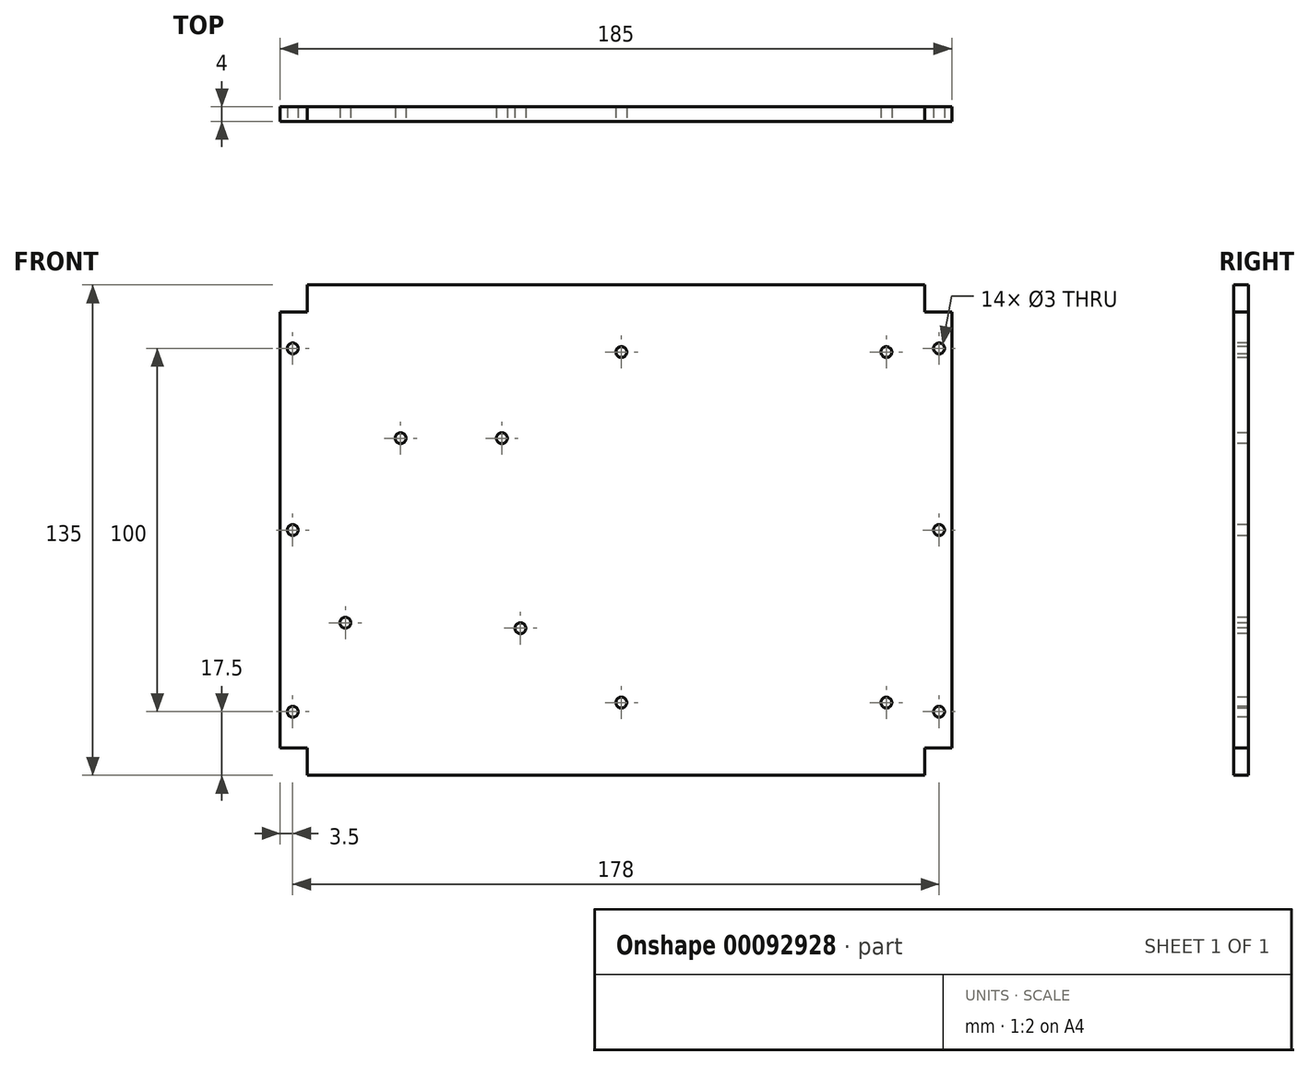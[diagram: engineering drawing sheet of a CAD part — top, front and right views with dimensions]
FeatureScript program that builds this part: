
annotation { "Feature Type Name" : "Feature", "Feature Type Description" : "" }
export const myFeature = defineFeature(function(context is Context, id is Id, definition is map)
    precondition{}
    {
        {
            var Q0;
            Q0=qCreatedBy(makeId("Front.planeOp"),FACE);
            var sketch = newSketch(context, id + "F0", { "sketchPlane" : qUnion([Q0])});
            skLineSegment(sketch, "E0.bottom", {"start": v(5, 0) * mm, "end": v(180, 0) * mm});
            skLineSegment(sketch, "E0.top", {"start": v(5, 135) * mm, "end": v(180, 135) * mm});
            skLineSegment(sketch, "E0.left", {"start": v(0, 5) * mm, "end": v(0, 130) * mm});
            skLineSegment(sketch, "E0.right", {"start": v(185, 5) * mm, "end": v(185, 130) * mm});
            skPoint(sketch, "E1.visualSharp", {"position": v(0, 135) * mm});
            skArc(sketch, "E1.filletArc", {"start": v(5, 135) * mm, "mid": v(1.46, 133.54) * mm, "end": v(0, 130) * mm});
            skPoint(sketch, "E2.visualSharp", {"position": v(185, 135) * mm});
            skArc(sketch, "E2.filletArc", {"start": v(185, 130) * mm, "mid": v(183.54, 133.54) * mm, "end": v(180, 135) * mm});
            skPoint(sketch, "E3.visualSharp", {"position": v(185, 0) * mm});
            skArc(sketch, "E3.filletArc", {"start": v(180, 0) * mm, "mid": v(183.54, 1.46) * mm, "end": v(185, 5) * mm});
            skPoint(sketch, "E4.visualSharp", {"position": v(0, 0) * mm});
            skArc(sketch, "E4.filletArc", {"start": v(0, 5) * mm, "mid": v(1.46, 1.46) * mm, "end": v(5, 0) * mm});
            skLineSegment(sketch, "E5", {"start": v(0, 67.5) * mm, "end": v(185, 67.5) * mm, "construction": true});
            skLineSegment(sketch, "E6", {"start": v(0, 127.5) * mm, "end": v(185, 127.5) * mm});
            skLineSegment(sketch, "E7", {"start": v(0, 7.5) * mm, "end": v(185, 7.5) * mm});
            skLineSegment(sketch, "E8", {"start": v(7.5, 135) * mm, "end": v(7.5, 0) * mm});
            skLineSegment(sketch, "E9", {"start": v(177.5, 135) * mm, "end": v(177.5, 0) * mm});
            skLineSegment(sketch, "E10", {"start": v(92.5, 135) * mm, "end": v(92.5, 0) * mm, "construction": true});
            skSolve(sketch);
        }
        {
            var Q0;
            Q0=makeQuery(id+"F0.imprint","IMPRINT",FACE,{"disambiguationData":[TD([[makeQuery(id+"F0.imprint","IMPRINT",EDGE,{"derivedFrom":sQuery(id+"F0.wireOp",EDGE,"E0.bottom")}),1.0]])]});
            var Q1;
            {var subQ0=sQuery(id+"F0.wireOp",EDGE,"E8");var subQ1=sQuery(id+"F0.wireOp",EDGE,"E6");var subQ2=makeQuery(id+"F0.imprint","INTERSECT",VERTEX,{"derivedFrom":[subQ1,subQ0]});Q1=makeQuery(id+"F0.imprint","IMPRINT",FACE,{"disambiguationData":[TD([[makeQuery(id+"F0.imprint","IMPRINT",EDGE,{"disambiguationData":[TD([[subQ2,-1.0]])],"derivedFrom":subQ1}),-1.0]])]});}
            var Q2;
            {var subQ0=sQuery(id+"F0.wireOp",EDGE,"E8");var subQ1=sQuery(id+"F0.wireOp",EDGE,"E0.top");var subQ2=makeQuery(id+"F0.imprint","INTERSECT",VERTEX,{"derivedFrom":[subQ1,subQ0]});Q2=makeQuery(id+"F0.imprint","IMPRINT",FACE,{"disambiguationData":[TD([[makeQuery(id+"F0.imprint","IMPRINT",EDGE,{"disambiguationData":[TD([[subQ2,-1.0]])],"derivedFrom":subQ1}),-1.0]])]});}
            var Q3;
            {var subQ0=sQuery(id+"F0.wireOp",EDGE,"E6");var subQ1=sQuery(id+"F0.wireOp",EDGE,"E0.left");var subQ2=makeQuery(id+"F0.imprint","INTERSECT",VERTEX,{"derivedFrom":[subQ1,subQ0]});Q3=makeQuery(id+"F0.imprint","IMPRINT",FACE,{"disambiguationData":[TD([[makeQuery(id+"F0.imprint","IMPRINT",EDGE,{"disambiguationData":[TD([[subQ2,1.0]])],"derivedFrom":subQ1}),-1.0]])]});}
            var Q4;
            {var subQ0=sQuery(id+"F0.wireOp",EDGE,"E6");var subQ1=sQuery(id+"F0.wireOp",EDGE,"E0.right");var subQ2=makeQuery(id+"F0.imprint","INTERSECT",VERTEX,{"derivedFrom":[subQ1,subQ0]});Q4=makeQuery(id+"F0.imprint","IMPRINT",FACE,{"disambiguationData":[TD([[makeQuery(id+"F0.imprint","IMPRINT",EDGE,{"disambiguationData":[TD([[subQ2,1.0]])],"derivedFrom":subQ1}),1.0]])]});}
            extrude(context, id + "F1", {"entities" : qUnion([Q0, Q1, Q2, Q3, Q4]), "depth" : 4 * mm});
        }
        {
            var Q0;
            Q0=makeQuery(id+"F1.opExtrude","CAP_FACE",FACE,{"disambiguationData":[OSD([sQuery(id+"F0.wireOp",EDGE,"E0.bottom"),sQuery(id+"F0.wireOp",EDGE,"E0.top"),sQuery(id+"F0.wireOp",EDGE,"E0.left"),sQuery(id+"F0.wireOp",EDGE,"E0.right"),sQuery(id+"F0.wireOp",EDGE,"E1.filletArc"),sQuery(id+"F0.wireOp",EDGE,"E2.filletArc"),sQuery(id+"F0.wireOp",EDGE,"E3.filletArc"),sQuery(id+"F0.wireOp",EDGE,"E4.filletArc")])],"isStart":false});
            var sketch = newSketch(context, id + "F2", { "sketchPlane" : qUnion([Q0])});
            skLineSegment(sketch, "E11", {"start": v(0, 67.5) * mm, "end": v(185, 67.5) * mm, "construction": true});
            skLineSegment(sketch, "E12", {"start": v(0, 117.5) * mm, "end": v(185, 117.5) * mm, "construction": true});
            skLineSegment(sketch, "E13", {"start": v(0, 17.5) * mm, "end": v(185, 17.5) * mm, "construction": true});
            skLineSegment(sketch, "E14", {"start": v(92.5, 135) * mm, "end": v(92.5, 0) * mm, "construction": true});
            skLineSegment(sketch, "E15", {"start": v(181.5, 135) * mm, "end": v(181.5, 0) * mm, "construction": true});
            skLineSegment(sketch, "E16", {"start": v(3.5, 135) * mm, "end": v(3.5, 0) * mm, "construction": true});
            skPoint(sketch, "E17", {"position": v(3.5, 67.5) * mm});
            skPoint(sketch, "E18", {"position": v(3.5, 17.5) * mm});
            skPoint(sketch, "E19", {"position": v(3.5, 117.5) * mm});
            skPoint(sketch, "E20", {"position": v(181.5, 117.5) * mm});
            skPoint(sketch, "E21", {"position": v(181.5, 67.5) * mm});
            skPoint(sketch, "E22", {"position": v(181.5, 17.5) * mm});
            skLineSegment(sketch, "E23", {"start": v(3.5, 117.5) * mm, "end": v(181.5, 117.5) * mm});
            skLineSegment(sketch, "E24", {"start": v(3.5, 67.5) * mm, "end": v(181.5, 67.5) * mm});
            skLineSegment(sketch, "E25", {"start": v(3.5, 17.5) * mm, "end": v(181.5, 17.5) * mm});
            skSolve(sketch);
        }
        {
            var Q0;
            Q0=sQuery(id+"F2.wireOp",VERTEX,"E19");
            var Q1;
            Q1=sQuery(id+"F2.wireOp",VERTEX,"E17");
            var Q2;
            Q2=sQuery(id+"F2.wireOp",VERTEX,"E18");
            var Q3;
            Q3=sQuery(id+"F2.wireOp",VERTEX,"E22");
            var Q4;
            Q4=sQuery(id+"F2.wireOp",VERTEX,"E21");
            var Q5;
            Q5=sQuery(id+"F2.wireOp",VERTEX,"E20");
            var Q6;
            Q6=makeQuery(id+"F1.opExtrude","SWEPT_BODY",BODY,{"disambiguationData":[OSD([sQuery(id+"F0.wireOp",EDGE,"E0.bottom"),sQuery(id+"F0.wireOp",EDGE,"E0.top"),sQuery(id+"F0.wireOp",EDGE,"E0.left"),sQuery(id+"F0.wireOp",EDGE,"E0.right"),sQuery(id+"F0.wireOp",EDGE,"E1.filletArc"),sQuery(id+"F0.wireOp",EDGE,"E2.filletArc"),sQuery(id+"F0.wireOp",EDGE,"E3.filletArc"),sQuery(id+"F0.wireOp",EDGE,"E4.filletArc")])]});
            hole(context, id + "F3", {"style" : HoleStyle.SIMPLE, "endStyle" : HoleEndStyle.THROUGH, "holeDiameter" : 3 * mm, "locations" : qUnion([Q0, Q1, Q2, Q3, Q4, Q5]), "scope" : qUnion([Q6]), "isTappedThrough" : true});
        }
        {
            var Q0;
            Q0=makeQuery(id+"F1.opExtrude","CAP_FACE",FACE,{"disambiguationData":[OSD([sQuery(id+"F0.wireOp",EDGE,"E0.bottom"),sQuery(id+"F0.wireOp",EDGE,"E0.top"),sQuery(id+"F0.wireOp",EDGE,"E0.left"),sQuery(id+"F0.wireOp",EDGE,"E0.right"),sQuery(id+"F0.wireOp",EDGE,"E6"),sQuery(id+"F0.wireOp",EDGE,"E7"),sQuery(id+"F0.wireOp",EDGE,"E8"),sQuery(id+"F0.wireOp",EDGE,"E9")])],"isStart":false});
            var sketch = newSketch(context, id + "F4", { "sketchPlane" : qUnion([Q0])});
            skLineSegment(sketch, "E26.bottom", {"start": v(94, 20) * mm, "end": v(167, 20) * mm});
            skLineSegment(sketch, "E26.top", {"start": v(94, 116.5) * mm, "end": v(167, 116.5) * mm});
            skLineSegment(sketch, "E26.left", {"start": v(94, 20) * mm, "end": v(94, 116.5) * mm});
            skLineSegment(sketch, "E26.right", {"start": v(167, 20) * mm, "end": v(167, 116.5) * mm});
            skSolve(sketch);
        }
        {
            var Q0;
            Q0=sQuery(id+"F4.wireOp",VERTEX,"E26.left.end");
            var Q1;
            Q1=sQuery(id+"F4.wireOp",VERTEX,"E26.right.end");
            var Q2;
            Q2=sQuery(id+"F4.wireOp",VERTEX,"E26.right.start");
            var Q3;
            Q3=sQuery(id+"F4.wireOp",VERTEX,"E26.bottom.start");
            var Q4;
            Q4=makeQuery(id+"F1.opExtrude","SWEPT_BODY",BODY,{"disambiguationData":[OSD([sQuery(id+"F0.wireOp",EDGE,"E0.bottom"),sQuery(id+"F0.wireOp",EDGE,"E0.top"),sQuery(id+"F0.wireOp",EDGE,"E0.left"),sQuery(id+"F0.wireOp",EDGE,"E0.right"),sQuery(id+"F0.wireOp",EDGE,"E6"),sQuery(id+"F0.wireOp",EDGE,"E7"),sQuery(id+"F0.wireOp",EDGE,"E8"),sQuery(id+"F0.wireOp",EDGE,"E9")])]});
            hole(context, id + "F5", {"style" : HoleStyle.SIMPLE, "endStyle" : HoleEndStyle.THROUGH, "holeDiameter" : 3 * mm, "locations" : qUnion([Q0, Q1, Q2, Q3]), "scope" : qUnion([Q4]), "isTappedThrough" : true});
        }
        {
            var Q0;
            Q0=makeQuery(id+"F1.opExtrude","CAP_FACE",FACE,{"disambiguationData":[OSD([sQuery(id+"F0.wireOp",EDGE,"E0.bottom"),sQuery(id+"F0.wireOp",EDGE,"E0.top"),sQuery(id+"F0.wireOp",EDGE,"E0.left"),sQuery(id+"F0.wireOp",EDGE,"E0.right"),sQuery(id+"F0.wireOp",EDGE,"E6"),sQuery(id+"F0.wireOp",EDGE,"E7"),sQuery(id+"F0.wireOp",EDGE,"E8"),sQuery(id+"F0.wireOp",EDGE,"E9")])],"isStart":false});
            var sketch = newSketch(context, id + "F6", { "sketchPlane" : qUnion([Q0])});
            skLineSegment(sketch, "E27", {"start": v(33.2, 92.8) * mm, "end": v(61.1, 92.8) * mm});
            skPoint(sketch, "E28", {"position": v(18, 42) * mm});
            skPoint(sketch, "E29", {"position": v(66.2, 40.5) * mm});
            skLineSegment(sketch, "E30", {"start": v(33.2, 92.8) * mm, "end": v(18, 42) * mm});
            skLineSegment(sketch, "E31", {"start": v(18, 42) * mm, "end": v(66.2, 40.5) * mm});
            skLineSegment(sketch, "E32", {"start": v(66.2, 40.5) * mm, "end": v(61.1, 92.8) * mm});
            skSolve(sketch);
        }
        {
            var Q0;
            Q0=sQuery(id+"F6.wireOp",VERTEX,"E28");
            var Q1;
            Q1=sQuery(id+"F6.wireOp",VERTEX,"E27.start");
            var Q2;
            Q2=sQuery(id+"F6.wireOp",VERTEX,"E27.end");
            var Q3;
            Q3=sQuery(id+"F6.wireOp",VERTEX,"E29");
            var Q4;
            Q4=makeQuery(id+"F1.opExtrude","SWEPT_BODY",BODY,{"disambiguationData":[OSD([sQuery(id+"F0.wireOp",EDGE,"E0.bottom"),sQuery(id+"F0.wireOp",EDGE,"E0.top"),sQuery(id+"F0.wireOp",EDGE,"E0.left"),sQuery(id+"F0.wireOp",EDGE,"E0.right"),sQuery(id+"F0.wireOp",EDGE,"E6"),sQuery(id+"F0.wireOp",EDGE,"E7"),sQuery(id+"F0.wireOp",EDGE,"E8"),sQuery(id+"F0.wireOp",EDGE,"E9")])]});
            hole(context, id + "F7", {"style" : HoleStyle.SIMPLE, "endStyle" : HoleEndStyle.THROUGH, "holeDiameter" : 3 * mm, "locations" : qUnion([Q0, Q1, Q2, Q3]), "scope" : qUnion([Q4]), "isTappedThrough" : true});
        }
    });
